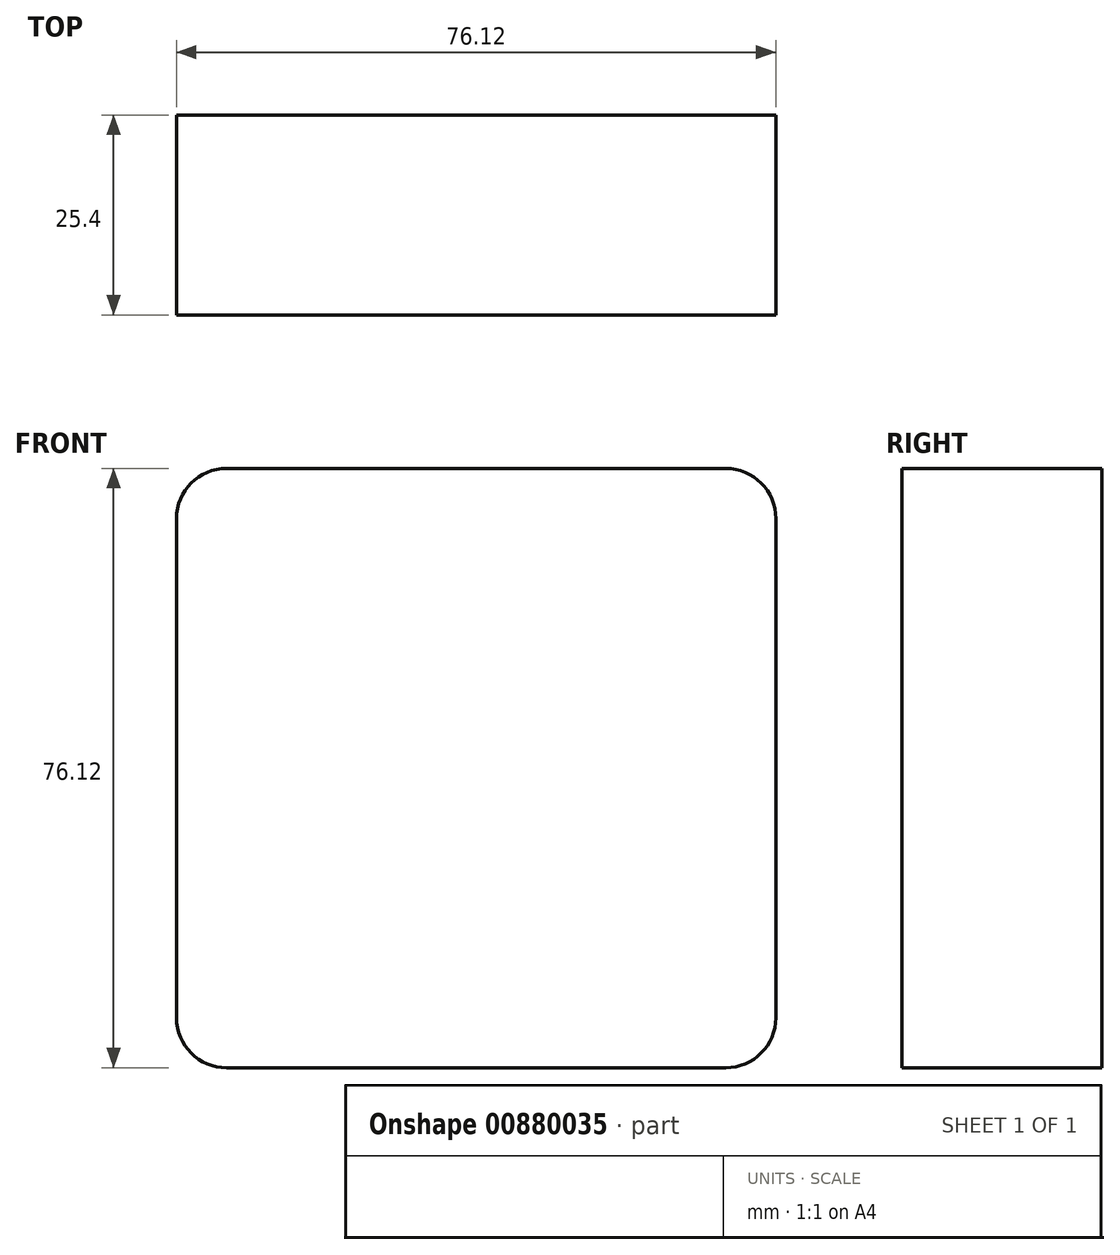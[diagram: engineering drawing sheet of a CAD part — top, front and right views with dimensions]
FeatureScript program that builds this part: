
annotation { "Feature Type Name" : "Feature", "Feature Type Description" : "" }
export const myFeature = defineFeature(function(context is Context, id is Id, definition is map)
    precondition{}
    {
        {
            var Q0;
            Q0=qCreatedBy(makeId("Front.planeOp"),FACE);
            var sketch = newSketch(context, id + "F0", { "sketchPlane" : qUnion([Q0])});
            skLineSegment(sketch, "E0.bottom", {"start": v(-6.35, 0) * mm, "end": v(-69.77, 0) * mm});
            skLineSegment(sketch, "E0.top", {"start": v(-6.35, 76.12) * mm, "end": v(-69.77, 76.12) * mm});
            skLineSegment(sketch, "E0.left", {"start": v(0, 6.35) * mm, "end": v(0, 69.77) * mm});
            skLineSegment(sketch, "E0.right", {"start": v(-76.12, 6.35) * mm, "end": v(-76.12, 69.77) * mm});
            skPoint(sketch, "E1.visualSharp", {"position": v(-76.12, 76.12) * mm});
            skArc(sketch, "E1.filletArc", {"start": v(-69.77, 76.12) * mm, "mid": v(-74.26, 74.26) * mm, "end": v(-76.12, 69.77) * mm});
            skPoint(sketch, "E2.visualSharp", {"position": v(0, 0) * mm});
            skArc(sketch, "E2.filletArc", {"start": v(-6.35, 0) * mm, "mid": v(-1.86, 1.86) * mm, "end": v(0, 6.35) * mm});
            skPoint(sketch, "E3.visualSharp", {"position": v(-76.12, 0) * mm});
            skArc(sketch, "E3.filletArc", {"start": v(-76.12, 6.35) * mm, "mid": v(-74.26, 1.86) * mm, "end": v(-69.77, 0) * mm});
            skPoint(sketch, "E4.visualSharp", {"position": v(0, 76.12) * mm});
            skArc(sketch, "E4.filletArc", {"start": v(0, 69.77) * mm, "mid": v(-1.86, 74.26) * mm, "end": v(-6.35, 76.12) * mm});
            skSolve(sketch);
        }
        {
            var Q0;
            Q0=makeQuery(id+"F0.imprint","IMPRINT",FACE,{"disambiguationData":[TD([[makeQuery(id+"F0.imprint","IMPRINT",EDGE,{"derivedFrom":sQuery(id+"F0.wireOp",EDGE,"E0.bottom")}),-1.0]])]});
            extrude(context, id + "F1", {"entities" : qUnion([Q0]), "depth" : 25.4 * mm, "offsetDistance" : 25.4 * mm});
        }
    });
